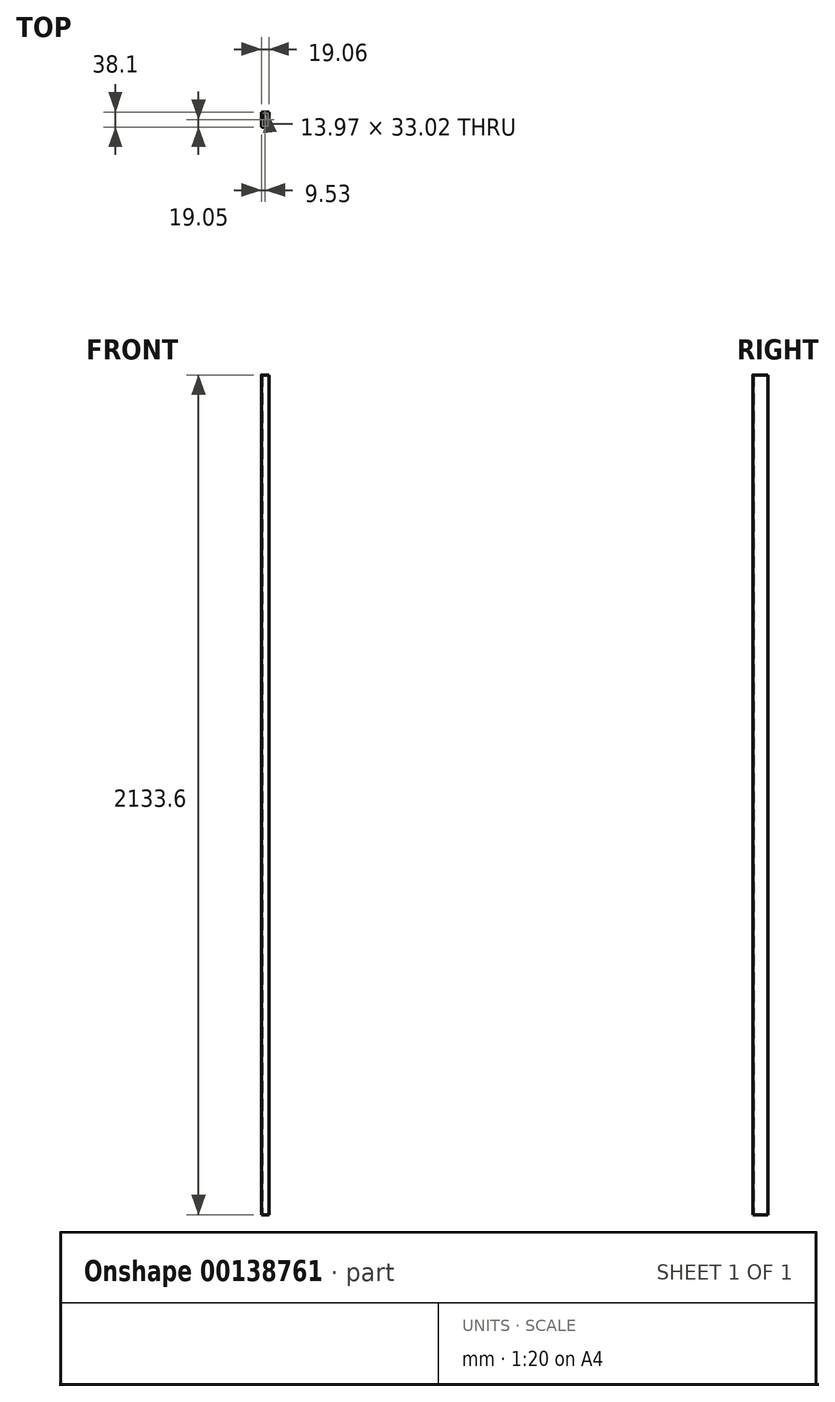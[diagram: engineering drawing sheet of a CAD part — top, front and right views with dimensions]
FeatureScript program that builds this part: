
annotation { "Feature Type Name" : "Feature", "Feature Type Description" : "" }
export const myFeature = defineFeature(function(context is Context, id is Id, definition is map)
    precondition{}
    {
        {
            var Q0;
            Q0=qCreatedBy(makeId("Top.planeOp"),FACE);
            var sketch = newSketch(context, id + "F0", { "sketchPlane" : qUnion([Q0])});
            skLineSegment(sketch, "E0.bottom", {"start": v(-8.02, 19.05) * mm, "end": v(8.03, 19.05) * mm});
            skLineSegment(sketch, "E0.top", {"start": v(-8.02, -19.05) * mm, "end": v(8.03, -19.05) * mm});
            skLineSegment(sketch, "E0.left", {"start": v(-9.53, 17.55) * mm, "end": v(-9.53, -17.55) * mm});
            skLineSegment(sketch, "E0.right", {"start": v(9.53, 17.55) * mm, "end": v(9.52, -17.55) * mm});
            skPoint(sketch, "E0.middle", {"position": v(0, 0) * mm});
            skPoint(sketch, "E1.visualSharp", {"position": v(-9.52, 19.05) * mm});
            skArc(sketch, "E1.filletArc", {"start": v(-8.02, 19.05) * mm, "mid": v(-9.09, 18.61) * mm, "end": v(-9.52, 17.55) * mm});
            skPoint(sketch, "E2.visualSharp", {"position": v(9.53, 19.05) * mm});
            skArc(sketch, "E2.filletArc", {"start": v(9.53, 17.55) * mm, "mid": v(9.09, 18.61) * mm, "end": v(8.03, 19.05) * mm});
            skPoint(sketch, "E3.visualSharp", {"position": v(9.52, -19.05) * mm});
            skArc(sketch, "E3.filletArc", {"start": v(8.03, -19.05) * mm, "mid": v(9.09, -18.61) * mm, "end": v(9.53, -17.55) * mm});
            skPoint(sketch, "E4.visualSharp", {"position": v(-9.53, -19.05) * mm});
            skArc(sketch, "E4.filletArc", {"start": v(-9.52, -17.55) * mm, "mid": v(-9.09, -18.61) * mm, "end": v(-8.02, -19.05) * mm});
            skLineSegment(sketch, "E5.0", {"start": v(-6.98, 16.5) * mm, "end": v(6.99, 16.5) * mm});
            skLineSegment(sketch, "E5.1", {"start": v(-6.98, 16.5) * mm, "end": v(-6.99, -16.51) * mm});
            skLineSegment(sketch, "E5.2", {"start": v(-6.99, -16.51) * mm, "end": v(6.98, -16.51) * mm});
            skLineSegment(sketch, "E5.3", {"start": v(6.99, 16.5) * mm, "end": v(6.98, -16.51) * mm});
            skSolve(sketch);
        }
        {
            var Q0;
            Q0=makeQuery(id+"F0.imprint","IMPRINT",FACE,{"disambiguationData":[TD([[makeQuery(id+"F0.imprint","IMPRINT",EDGE,{"derivedFrom":sQuery(id+"F0.wireOp",EDGE,"E0.bottom")}),-1.0]])]});
            extrude(context, id + "F1", {"entities" : qUnion([Q0]), "depth" : 13.5 * 152.4 * mm + 76.2 * mm});
        }
    });
